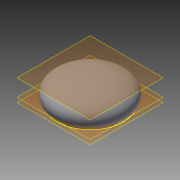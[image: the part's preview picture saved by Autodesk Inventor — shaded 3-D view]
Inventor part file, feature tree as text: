
AUTODESK INVENTOR PART (.ipt)
format: ipt  version: 2014 (Build 180170000, 170)  size: 167,424 bytes
history: native  units: mm
features: reference x8, sketch x5, plane x3, loft x1, extrude x1, projected_geometry x1
ambient origin geometry x8: Origin, YZ Plane, XZ Plane, XY Plane, X Axis, Y Axis, Z Axis, Center Point
bodies: Solid1 (feature_tree)
feature tree (19):
  plane  "Work Plane1"
  sketch  "Sketch2"  dims[d0=20.0mm d1=150.0mm]
  plane  "Work Plane2"
  sketch  "Sketch3"  dims[d2=0.0mm d3=90.0deg d4=0.0mm d5=90.0deg]
  plane  "Work Plane3"
  loft  "Loft1"
  extrude  "Extrusion1"  TaperAngle=0.0deg  [1 undecoded]
  sketch  "Sketch6"  dims[d9=30.0mm d10=0.0mm]
  sketch  "Sketch4"  dims[d6=0.0mm d7=90.0deg]
  sketch  "Sketch5"  dims[d8=115.0mm]
  reference  "Reference2"
  reference  "Reference3"
  reference  "Reference4"
  reference  "Reference5"
  reference  "Reference6"
  reference  "Reference7"
  projected_geometry  "Projected Loop1"
  reference  "Reference8"
  reference  "Reference9"
note: 1 required parameter value undecoded (feature->parameter linkage not recoverable at this tier; creation-order binding heuristic only, values carry confidence <= 0.55)
